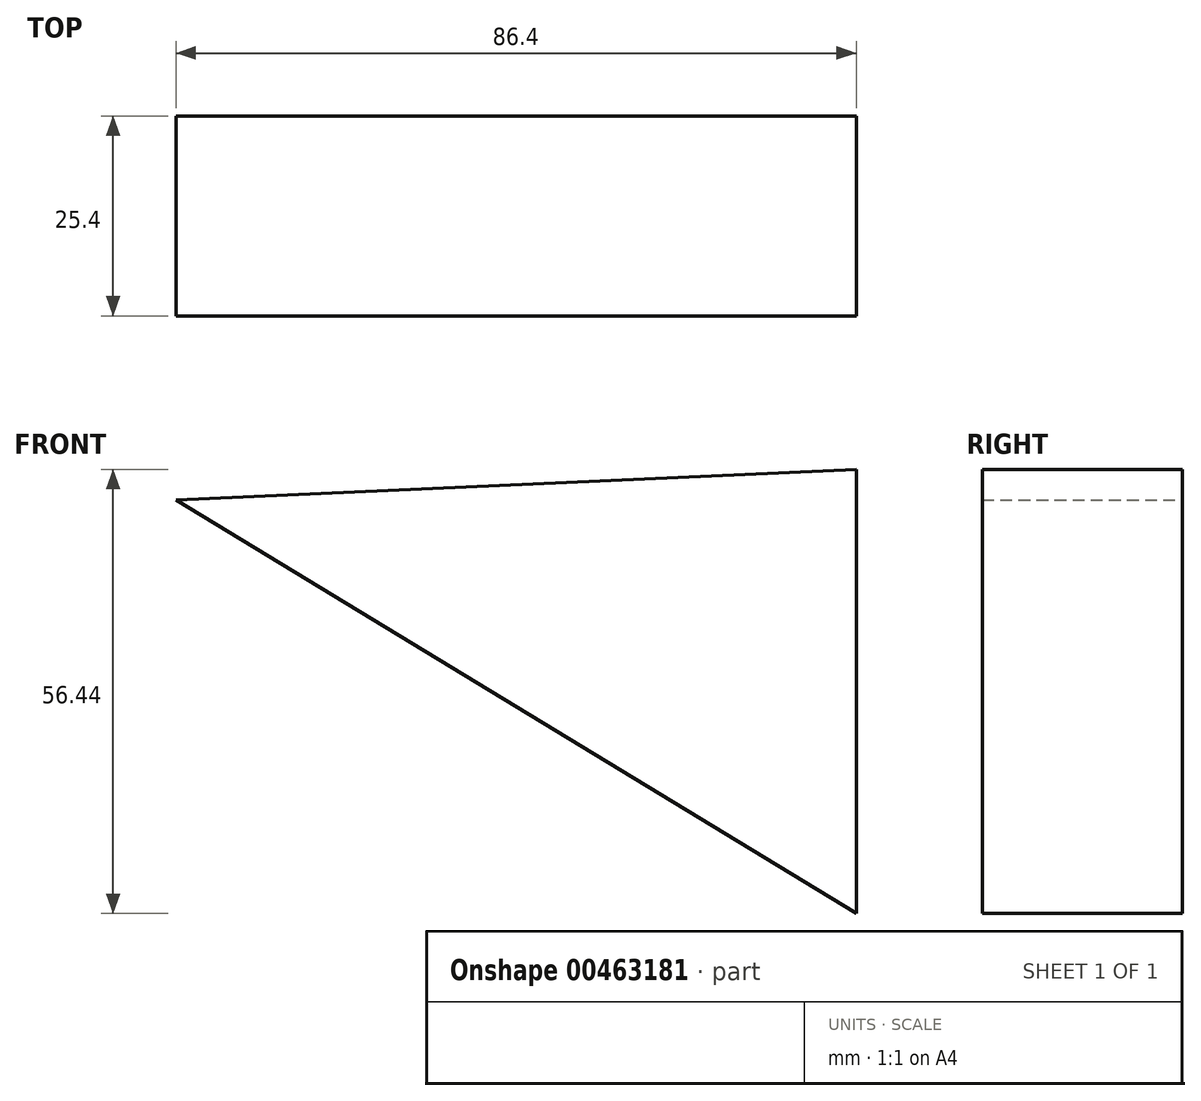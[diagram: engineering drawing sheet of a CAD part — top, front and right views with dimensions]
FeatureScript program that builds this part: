
annotation { "Feature Type Name" : "Feature", "Feature Type Description" : "" }
export const myFeature = defineFeature(function(context is Context, id is Id, definition is map)
    precondition{}
    {
        {
            var Q0;
            Q0=qCreatedBy(makeId("Front.planeOp"),FACE);
            var sketch = newSketch(context, id + "F0", { "sketchPlane" : qUnion([Q0])});
            skLineSegment(sketch, "E0", {"start": v(-66.6, 46.72) * mm, "end": v(19.79, -5.83) * mm});
            skLineSegment(sketch, "E1", {"start": v(19.79, -5.83) * mm, "end": v(19.79, 50.6) * mm});
            skLineSegment(sketch, "E2", {"start": v(19.79, 50.6) * mm, "end": v(-66.6, 46.72) * mm});
            skSolve(sketch);
        }
        {
            var Q0;
            Q0=makeQuery(id+"F0.imprint","IMPRINT",FACE,{"disambiguationData":[TD([[makeQuery(id+"F0.imprint","IMPRINT",EDGE,{"derivedFrom":sQuery(id+"F0.wireOp",EDGE,"E0")}),1.0]])]});
            extrude(context, id + "F1", {"entities" : qUnion([Q0]), "depth" : 25.4 * mm});
        }
    });
